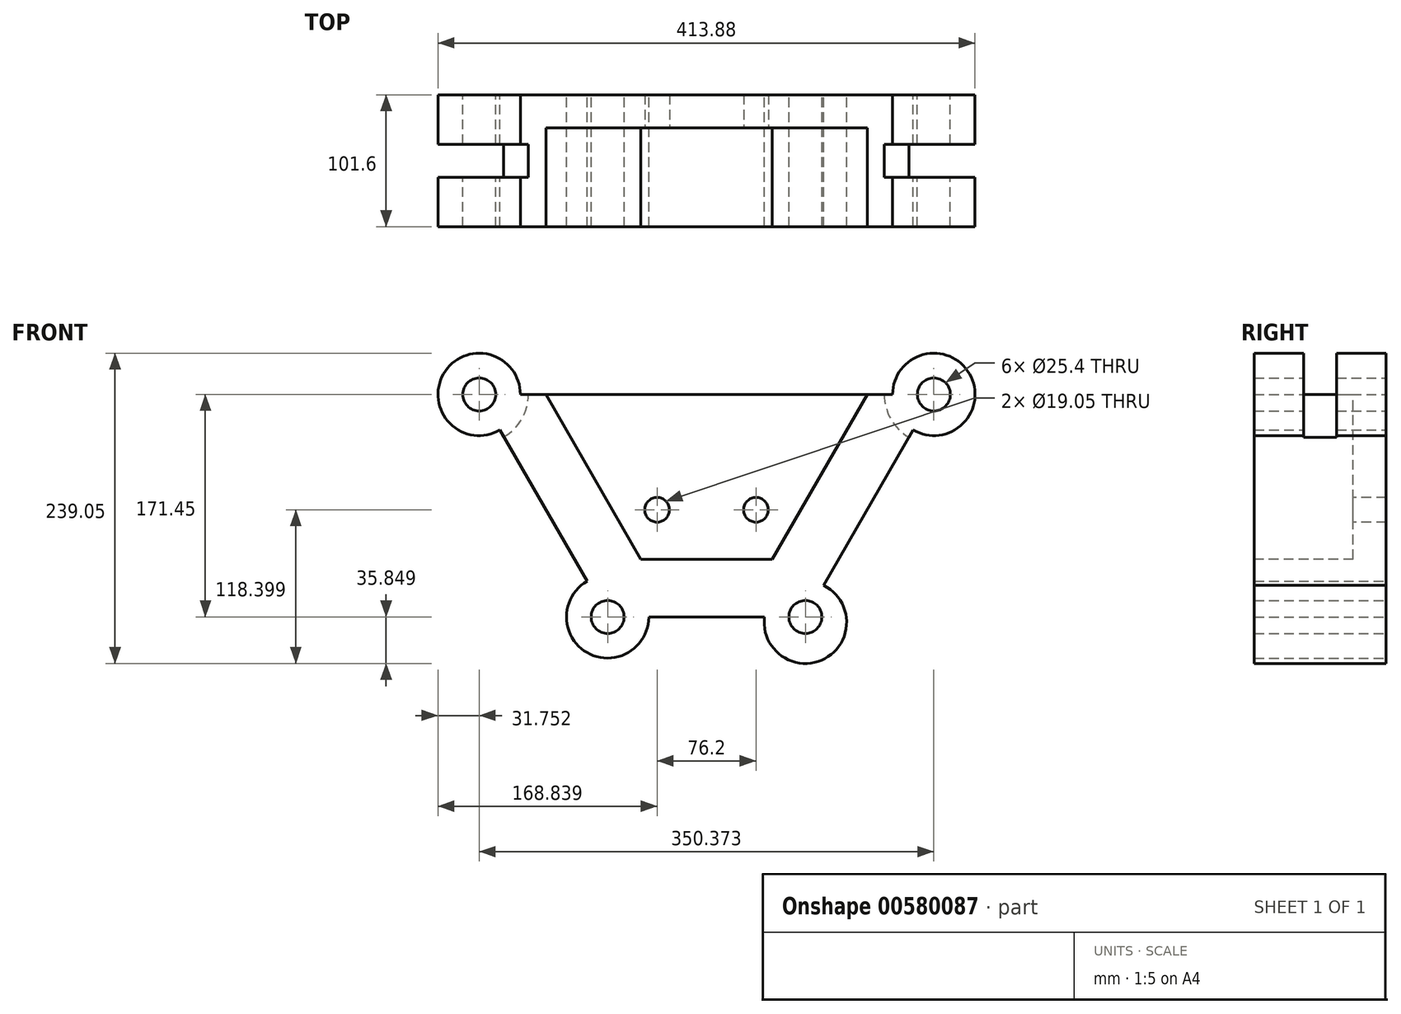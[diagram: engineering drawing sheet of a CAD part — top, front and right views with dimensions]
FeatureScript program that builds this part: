
annotation { "Feature Type Name" : "Feature", "Feature Type Description" : "" }
export const myFeature = defineFeature(function(context is Context, id is Id, definition is map)
    precondition{}
    {
        {
            var Q0;
            Q0=qCreatedBy(makeId("Front.planeOp"),FACE);
            var sketch = newSketch(context, id + "F0", { "sketchPlane" : qUnion([Q0])});
            skLineSegment(sketch, "E0", {"start": v(-13.75, -131.84) * mm, "end": v(138.65, -131.84) * mm});
            skLineSegment(sketch, "E1", {"start": v(-112.74, 39.6) * mm, "end": v(237.64, 39.6) * mm});
            skLineSegment(sketch, "E2", {"start": v(-112.74, 39.6) * mm, "end": v(-13.75, -131.84) * mm});
            skLineSegment(sketch, "E3", {"start": v(237.64, 39.6) * mm, "end": v(138.65, -131.84) * mm});
            skCircle(sketch, "E4", {"center": v(237.64, 39.6) * mm, "radius": 12.7 * mm});
            skCircle(sketch, "E5", {"center": v(237.64, 39.6) * mm, "radius": 31.75 * mm});
            skCircle(sketch, "E6", {"center": v(-112.74, 39.6) * mm, "radius": 12.7 * mm});
            skCircle(sketch, "E7", {"center": v(-112.74, 39.6) * mm, "radius": 31.75 * mm});
            skCircle(sketch, "E8", {"center": v(-13.75, -131.84) * mm, "radius": 12.7 * mm});
            skCircle(sketch, "E9", {"center": v(-13.75, -131.84) * mm, "radius": 31.75 * mm});
            skCircle(sketch, "E10", {"center": v(138.65, -131.84) * mm, "radius": 12.7 * mm});
            skCircle(sketch, "E11", {"center": v(138.65, -135.94) * mm, "radius": 31.75 * mm});
            skLineSegment(sketch, "E12", {"start": v(62.45, 39.6) * mm, "end": v(62.45, -131.84) * mm});
            skLineSegment(sketch, "E13", {"start": v(-96.86, 12.11) * mm, "end": v(-13.75, -131.84) * mm});
            skLineSegment(sketch, "E14", {"start": v(138.65, -131.84) * mm, "end": v(221.76, 12.11) * mm});
            skLineSegment(sketch, "E15", {"start": v(-13.75, -131.84) * mm, "end": v(-96.86, 12.11) * mm});
            skSolve(sketch);
        }
        {
            var Q0;
            {var subQ0=sQuery(id+"F0.wireOp",EDGE,"E7");var subQ1=sQuery(id+"F0.wireOp",EDGE,"E1");var subQ2=makeQuery(id+"F0.imprint","INTERSECT",VERTEX,{"derivedFrom":[subQ1,subQ0]});Q0=makeQuery(id+"F0.imprint","IMPRINT",FACE,{"disambiguationData":[TD([[makeQuery(id+"F0.imprint","IMPRINT",EDGE,{"disambiguationData":[TD([[subQ2,1.0]])],"derivedFrom":subQ1}),1.0]])]});}
            var Q1;
            {var subQ0=sQuery(id+"F0.wireOp",EDGE,"E7");var subQ1=sQuery(id+"F0.wireOp",EDGE,"E1");var subQ2=makeQuery(id+"F0.imprint","INTERSECT",VERTEX,{"derivedFrom":[subQ1,subQ0]});Q1=makeQuery(id+"F0.imprint","IMPRINT",FACE,{"disambiguationData":[TD([[makeQuery(id+"F0.imprint","IMPRINT",EDGE,{"disambiguationData":[TD([[subQ2,1.0]])],"derivedFrom":subQ1}),-1.0]])]});}
            var Q2;
            {var subQ7=sQuery(id+"F0.wireOp",EDGE,"E12");Q2=makeQuery(id+"F0.imprint","IMPRINT",FACE,{"disambiguationData":[TD([[makeQuery(id+"F0.imprint","IMPRINT",EDGE,{"derivedFrom":subQ7}),-1.0]])]});}
            var Q3;
            {var subQ7=sQuery(id+"F0.wireOp",EDGE,"E12");Q3=makeQuery(id+"F0.imprint","IMPRINT",FACE,{"disambiguationData":[TD([[makeQuery(id+"F0.imprint","IMPRINT",EDGE,{"derivedFrom":subQ7}),1.0]])]});}
            var Q4;
            {var subQ0=sQuery(id+"F0.wireOp",EDGE,"E9");var subQ1=sQuery(id+"F0.wireOp",EDGE,"E0");var subQ2=makeQuery(id+"F0.imprint","INTERSECT",VERTEX,{"derivedFrom":[subQ1,subQ0]});Q4=makeQuery(id+"F0.imprint","IMPRINT",FACE,{"disambiguationData":[TD([[makeQuery(id+"F0.imprint","IMPRINT",EDGE,{"disambiguationData":[TD([[subQ2,1.0]])],"derivedFrom":subQ1}),1.0]])]});}
            var Q5;
            {var subQ0=sQuery(id+"F0.wireOp",EDGE,"E9");var subQ1=sQuery(id+"F0.wireOp",EDGE,"E0");var subQ2=makeQuery(id+"F0.imprint","INTERSECT",VERTEX,{"derivedFrom":[subQ1,subQ0]});Q5=makeQuery(id+"F0.imprint","IMPRINT",FACE,{"disambiguationData":[TD([[makeQuery(id+"F0.imprint","IMPRINT",EDGE,{"disambiguationData":[TD([[subQ2,1.0]])],"derivedFrom":subQ1}),-1.0]])]});}
            var Q6;
            {var subQ0=sQuery(id+"F0.wireOp",EDGE,"E11");var subQ1=sQuery(id+"F0.wireOp",EDGE,"E0");var subQ2=makeQuery(id+"F0.imprint","INTERSECT",VERTEX,{"derivedFrom":[subQ1,subQ0]});Q6=makeQuery(id+"F0.imprint","IMPRINT",FACE,{"disambiguationData":[TD([[makeQuery(id+"F0.imprint","IMPRINT",EDGE,{"disambiguationData":[TD([[subQ2,-1.0]])],"derivedFrom":subQ1}),-1.0]])]});}
            var Q7;
            {var subQ0=sQuery(id+"F0.wireOp",EDGE,"E11");var subQ1=sQuery(id+"F0.wireOp",EDGE,"E0");var subQ2=makeQuery(id+"F0.imprint","INTERSECT",VERTEX,{"derivedFrom":[subQ1,subQ0]});Q7=makeQuery(id+"F0.imprint","IMPRINT",FACE,{"disambiguationData":[TD([[makeQuery(id+"F0.imprint","IMPRINT",EDGE,{"disambiguationData":[TD([[subQ2,-1.0]])],"derivedFrom":subQ1}),1.0]])]});}
            var Q8;
            {var subQ0=sQuery(id+"F0.wireOp",EDGE,"E5");var subQ1=sQuery(id+"F0.wireOp",EDGE,"E1");var subQ2=makeQuery(id+"F0.imprint","INTERSECT",VERTEX,{"derivedFrom":[subQ1,subQ0]});Q8=makeQuery(id+"F0.imprint","IMPRINT",FACE,{"disambiguationData":[TD([[makeQuery(id+"F0.imprint","IMPRINT",EDGE,{"disambiguationData":[TD([[subQ2,-1.0]])],"derivedFrom":subQ1}),1.0]])]});}
            var Q9;
            {var subQ0=sQuery(id+"F0.wireOp",EDGE,"E5");var subQ1=sQuery(id+"F0.wireOp",EDGE,"E1");var subQ2=makeQuery(id+"F0.imprint","INTERSECT",VERTEX,{"derivedFrom":[subQ1,subQ0]});Q9=makeQuery(id+"F0.imprint","IMPRINT",FACE,{"disambiguationData":[TD([[makeQuery(id+"F0.imprint","IMPRINT",EDGE,{"disambiguationData":[TD([[subQ2,-1.0]])],"derivedFrom":subQ1}),-1.0]])]});}
            extrude(context, id + "F1", {"entities" : qUnion([Q0, Q1, Q2, Q3, Q4, Q5, Q6, Q7, Q8, Q9]), "endBound" : BoundingType.SYMMETRIC, "depth" : 101.6 * mm, "offsetDistance" : 25.4 * mm});
        }
        {
            var Q0;
            Q0=makeQuery(id+"F1.opExtrude","CAP_FACE",FACE,{"disambiguationData":[OSD([sQuery(id+"F0.wireOp",EDGE,"E1"),sQuery(id+"F0.wireOp",EDGE,"E4"),sQuery(id+"F0.wireOp",EDGE,"E5"),sQuery(id+"F0.wireOp",EDGE,"E6"),sQuery(id+"F0.wireOp",EDGE,"E7"),sQuery(id+"F0.wireOp",EDGE,"E9"),sQuery(id+"F0.wireOp",EDGE,"E11"),sQuery(id+"F0.wireOp",EDGE,"E0"),sQuery(id+"F0.wireOp",EDGE,"E14"),sQuery(id+"F0.wireOp",EDGE,"E15")])],"isStart":false});
            var sketch = newSketch(context, id + "F2", { "sketchPlane" : qUnion([Q0])});
            skLineSegment(sketch, "E16.0", {"start": v(11.91, -87.4) * mm, "end": v(-63.98, 44.05) * mm});
            skLineSegment(sketch, "E16.1", {"start": v(11.91, -87.4) * mm, "end": v(112.99, -87.4) * mm});
            skLineSegment(sketch, "E16.2", {"start": v(112.99, -87.4) * mm, "end": v(188.62, 43.6) * mm});
            skLineSegment(sketch, "E17", {"start": v(-63.98, 44.05) * mm, "end": v(188.62, 43.6) * mm});
            skSolve(sketch);
        }
        {
            var Q0;
            {var subQ0=sQuery(id+"F0.wireOp",EDGE,"E0");var subQ1=sQuery(id+"F0.wireOp",EDGE,"E8");var subQ2=makeQuery(id+"F0.imprint","INTERSECT",VERTEX,{"derivedFrom":[subQ1,subQ0]});Q0=makeQuery(id+"F0.imprint","IMPRINT",FACE,{"disambiguationData":[TD([[makeQuery(id+"F0.imprint","IMPRINT",EDGE,{"disambiguationData":[TD([[subQ2,-1.0]])],"derivedFrom":subQ1}),-1.0]])]});}
            var Q1;
            {var subQ0=sQuery(id+"F0.wireOp",EDGE,"E0");var subQ1=sQuery(id+"F0.wireOp",EDGE,"E8");var subQ2=makeQuery(id+"F0.imprint","INTERSECT",VERTEX,{"derivedFrom":[subQ1,subQ0]});Q1=makeQuery(id+"F0.imprint","IMPRINT",FACE,{"disambiguationData":[TD([[makeQuery(id+"F0.imprint","IMPRINT",EDGE,{"disambiguationData":[TD([[subQ2,1.0]])],"derivedFrom":subQ1}),-1.0]])]});}
            var Q2;
            {var subQ0=sQuery(id+"F0.wireOp",EDGE,"E0");var subQ1=sQuery(id+"F0.wireOp",EDGE,"E10");var subQ2=makeQuery(id+"F0.imprint","INTERSECT",VERTEX,{"derivedFrom":[subQ1,subQ0]});Q2=makeQuery(id+"F0.imprint","IMPRINT",FACE,{"disambiguationData":[TD([[makeQuery(id+"F0.imprint","IMPRINT",EDGE,{"disambiguationData":[TD([[subQ2,1.0]])],"derivedFrom":subQ1}),-1.0]])]});}
            var Q3;
            {var subQ0=sQuery(id+"F0.wireOp",EDGE,"E0");var subQ1=sQuery(id+"F0.wireOp",EDGE,"E10");var subQ2=makeQuery(id+"F0.imprint","INTERSECT",VERTEX,{"derivedFrom":[subQ1,subQ0]});Q3=makeQuery(id+"F0.imprint","IMPRINT",FACE,{"disambiguationData":[TD([[makeQuery(id+"F0.imprint","IMPRINT",EDGE,{"disambiguationData":[TD([[subQ2,-1.0]])],"derivedFrom":subQ1}),-1.0]])]});}
            extrude(context, id + "F3", {"entities" : qUnion([Q0, Q1, Q2, Q3]), "operationType" : NewBodyOperationType.ADD, "endBound" : BoundingType.SYMMETRIC, "depth" : 101.6 * mm, "offsetDistance" : 25.4 * mm});
        }
        {
            var Q0;
            Q0=makeQuery(id+"F2.imprint","IMPRINT",FACE,{"disambiguationData":[TD([[makeQuery(id+"F2.imprint","IMPRINT",EDGE,{"derivedFrom":sQuery(id+"F2.wireOp",EDGE,"E16.0")}),-1.0]])]});
            extrude(context, id + "F4", {"entities" : qUnion([Q0]), "operationType" : NewBodyOperationType.REMOVE, "oppositeDirection" : true, "depth" : 76.2 * mm, "offsetDistance" : 25.4 * mm});
        }
        {
            var Q0;
            Q0=qCreatedBy(makeId("Front.planeOp"),FACE);
            var sketch = newSketch(context, id + "F5", { "sketchPlane" : qUnion([Q0])});
            skCircle(sketch, "E18", {"center": v(-112.86, 39.84) * mm, "radius": 38.1 * mm});
            skCircle(sketch, "E19", {"center": v(237.59, 39.46) * mm, "radius": 38.1 * mm});
            skCircle(sketch, "E20", {"center": v(-13.85, -131.65) * mm, "radius": 38.1 * mm});
            skCircle(sketch, "E21", {"center": v(138.39, -135.9) * mm, "radius": 38.1 * mm});
            skSolve(sketch);
        }
        {
            var Q0;
            Q0=makeQuery(id+"F5.imprint","IMPRINT",FACE,{"disambiguationData":[TD([[makeQuery(id+"F5.imprint","IMPRINT",EDGE,{"derivedFrom":sQuery(id+"F5.wireOp",EDGE,"E19")}),1.0]])]});
            var Q1;
            Q1=makeQuery(id+"F5.imprint","IMPRINT",FACE,{"disambiguationData":[TD([[makeQuery(id+"F5.imprint","IMPRINT",EDGE,{"derivedFrom":sQuery(id+"F5.wireOp",EDGE,"E18")}),1.0]])]});
            var Q2;
            Q2=sQuery(id+"F5.wireOp",EDGE,"E18");
            var Q3;
            Q3=sQuery(id+"F5.wireOp",EDGE,"E20");
            var Q4;
            Q4=sQuery(id+"F5.wireOp",EDGE,"E21");
            var Q5;
            Q5=sQuery(id+"F5.wireOp",EDGE,"E19");
            extrude(context, id + "F6", {"entities" : qUnion([Q0, Q1]), "operationType" : NewBodyOperationType.REMOVE, "surfaceEntities" : qUnion([Q2, Q3, Q4, Q5]), "endBound" : BoundingType.SYMMETRIC, "depth" : 25.4 * mm, "offsetDistance" : 25.4 * mm});
        }
        {
            var Q0;
            {var subQ0=sQuery(id+"F0.wireOp",EDGE,"E11");var subQ1=sQuery(id+"F0.wireOp",EDGE,"E9");Q0=makeQuery(id+"F3.boolean.opBoolean","MERGE",FACE,{"derivedFrom":[makeQuery(id+"F1.opExtrude","CAP_FACE",FACE,{"disambiguationData":[OSD([sQuery(id+"F0.wireOp",EDGE,"E1"),sQuery(id+"F0.wireOp",EDGE,"E4"),sQuery(id+"F0.wireOp",EDGE,"E5"),sQuery(id+"F0.wireOp",EDGE,"E6"),sQuery(id+"F0.wireOp",EDGE,"E7"),subQ1,subQ0,sQuery(id+"F0.wireOp",EDGE,"E0"),sQuery(id+"F0.wireOp",EDGE,"E14"),sQuery(id+"F0.wireOp",EDGE,"E15")])],"isStart":false}),makeQuery(id+"F3.opExtrude","CAP_FACE",FACE,{"disambiguationData":[OSD([sQuery(id+"F0.wireOp",EDGE,"E8"),subQ1])],"isStart":false}),makeQuery(id+"F3.opExtrude","CAP_FACE",FACE,{"disambiguationData":[OSD([sQuery(id+"F0.wireOp",EDGE,"E10"),subQ0])],"isStart":false})]});}
            var sketch = newSketch(context, id + "F7", { "sketchPlane" : qUnion([Q0])});
            skLineSegment(sketch, "E22", {"start": v(62.45, -87.4) * mm, "end": v(62.45, -49.3) * mm});
            skLineSegment(sketch, "E23", {"start": v(62.45, -49.3) * mm, "end": v(100.55, -49.3) * mm});
            skLineSegment(sketch, "E24", {"start": v(62.45, -49.3) * mm, "end": v(24.35, -49.3) * mm});
            skCircle(sketch, "E25", {"center": v(100.55, -49.3) * mm, "radius": 9.52 * mm});
            skCircle(sketch, "E26", {"center": v(24.35, -49.3) * mm, "radius": 9.53 * mm});
            skSolve(sketch);
        }
        {
            var Q0;
            Q0=makeQuery(id+"F7.imprint","IMPRINT",FACE,{"disambiguationData":[TD([[makeQuery(id+"F7.imprint","IMPRINT",EDGE,{"derivedFrom":sQuery(id+"F7.wireOp",EDGE,"E26")}),1.0]])]});
            var Q1;
            Q1=makeQuery(id+"F7.imprint","IMPRINT",FACE,{"disambiguationData":[TD([[makeQuery(id+"F7.imprint","IMPRINT",EDGE,{"derivedFrom":sQuery(id+"F7.wireOp",EDGE,"E25")}),1.0]])]});
            var Q2;
            Q2=sQuery(id+"F7.wireOp",EDGE,"E26");
            var Q3;
            Q3=sQuery(id+"F7.wireOp",EDGE,"E24");
            var Q4;
            Q4=sQuery(id+"F7.wireOp",EDGE,"E22");
            var Q5;
            Q5=sQuery(id+"F7.wireOp",EDGE,"E23");
            var Q6;
            Q6=sQuery(id+"F7.wireOp",EDGE,"E25");
            extrude(context, id + "F8", {"entities" : qUnion([Q0, Q1]), "operationType" : NewBodyOperationType.REMOVE, "surfaceEntities" : qUnion([Q2, Q3, Q4, Q5, Q6]), "endBound" : BoundingType.THROUGH_ALL, "oppositeDirection" : true, "depth" : 25.4 * mm, "offsetDistance" : 25.4 * mm});
        }
    });
